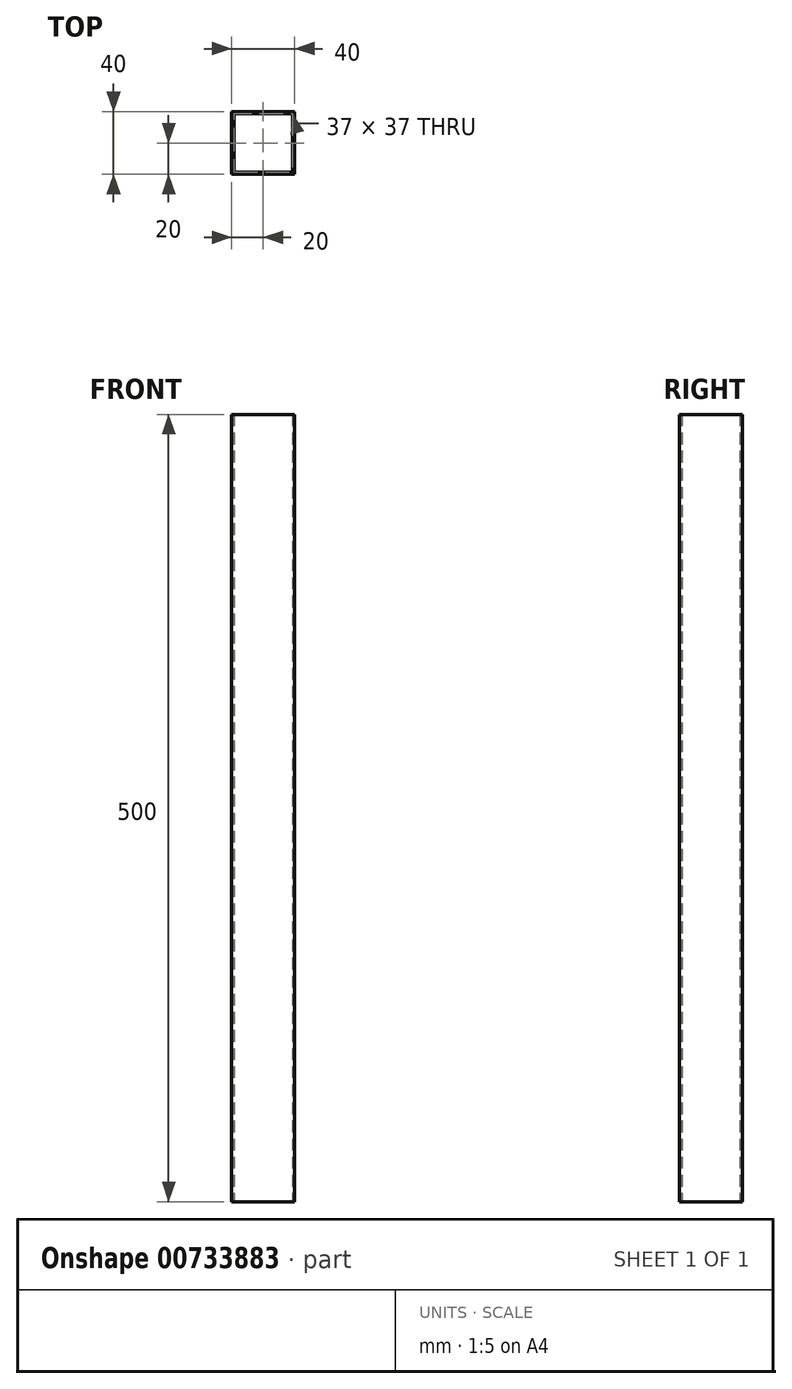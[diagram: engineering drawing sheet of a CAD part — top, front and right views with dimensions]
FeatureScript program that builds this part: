
annotation { "Feature Type Name" : "Feature", "Feature Type Description" : "" }
export const myFeature = defineFeature(function(context is Context, id is Id, definition is map)
    precondition{}
    {
        {
            var Q0;
            Q0=qCreatedBy(makeId("Top.planeOp"),FACE);
            var sketch = newSketch(context, id + "F0", { "sketchPlane" : qUnion([Q0])});
            skLineSegment(sketch, "E0.bottom", {"start": v(20, 20) * mm, "end": v(-20, 20) * mm});
            skLineSegment(sketch, "E0.top", {"start": v(20, -20) * mm, "end": v(-20, -20) * mm});
            skLineSegment(sketch, "E0.left", {"start": v(20, 20) * mm, "end": v(20, -20) * mm});
            skLineSegment(sketch, "E0.right", {"start": v(-20, 20) * mm, "end": v(-20, -20) * mm});
            skPoint(sketch, "E0.middle", {"position": v(0, 0) * mm});
            skLineSegment(sketch, "E1.bottom", {"start": v(18.5, 18.5) * mm, "end": v(-18.5, 18.5) * mm});
            skLineSegment(sketch, "E1.top", {"start": v(18.5, -18.5) * mm, "end": v(-18.5, -18.5) * mm});
            skLineSegment(sketch, "E1.left", {"start": v(18.5, 18.5) * mm, "end": v(18.5, -18.5) * mm});
            skLineSegment(sketch, "E1.right", {"start": v(-18.5, 18.5) * mm, "end": v(-18.5, -18.5) * mm});
            skSolve(sketch);
        }
        {
            var Q0;
            Q0=makeQuery(id+"F0.imprint","IMPRINT",FACE,{"disambiguationData":[TD([[makeQuery(id+"F0.imprint","IMPRINT",EDGE,{"derivedFrom":sQuery(id+"F0.wireOp",EDGE,"E0.bottom")}),1.0]])]});
            extrude(context, id + "F1", {"entities" : qUnion([Q0]), "depth" : 500 * mm, "offsetDistance" : 25 * mm});
        }
    });
